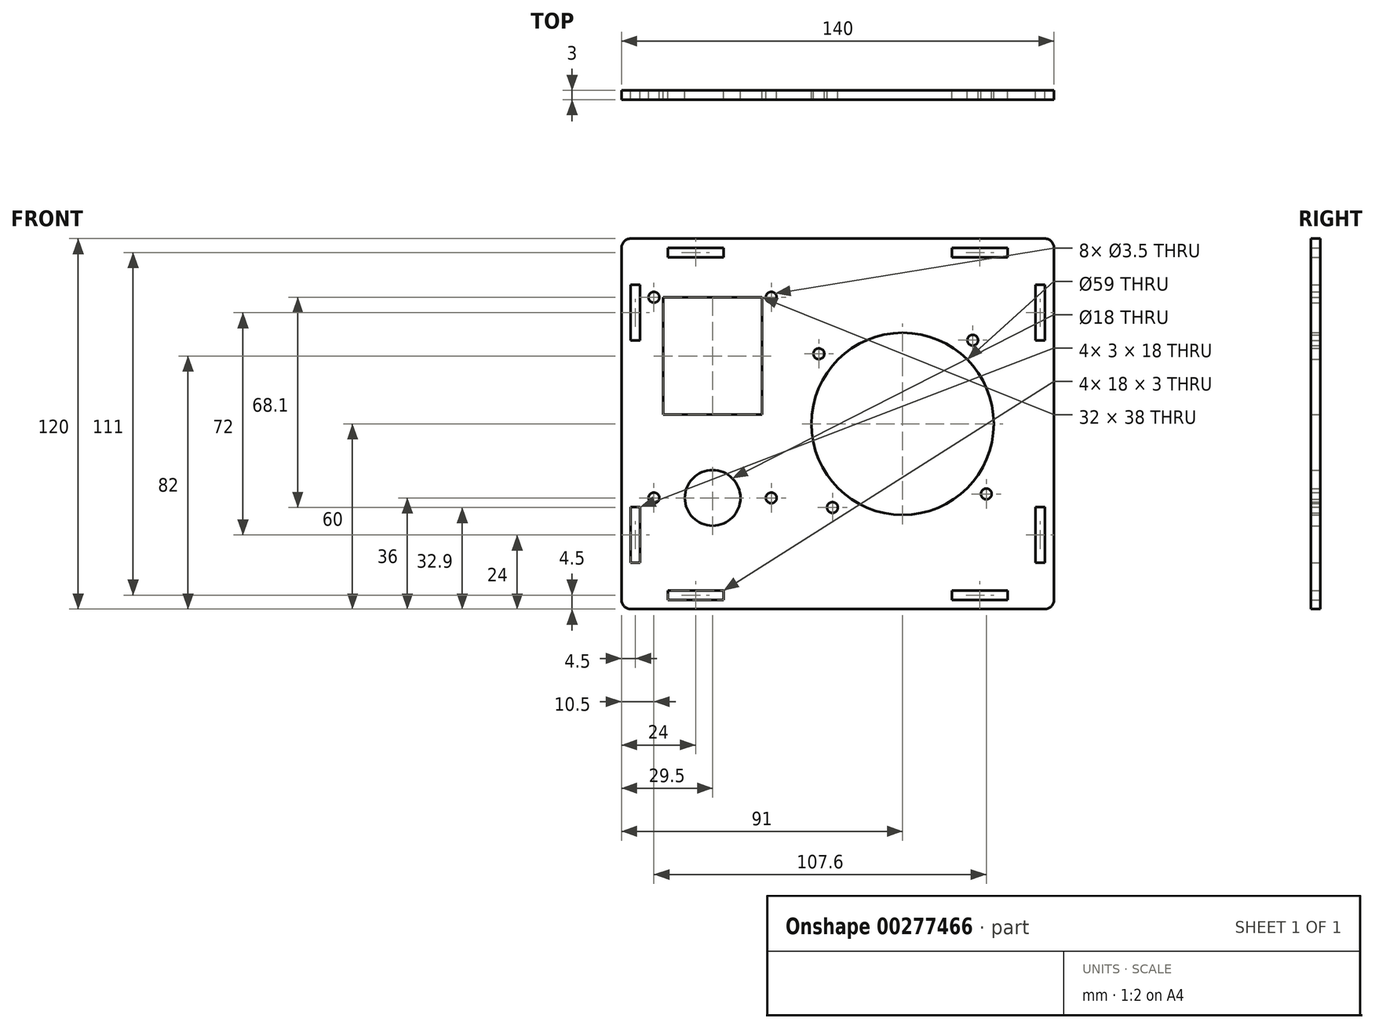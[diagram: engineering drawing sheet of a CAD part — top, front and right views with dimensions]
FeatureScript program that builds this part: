
annotation { "Feature Type Name" : "Feature", "Feature Type Description" : "" }
export const myFeature = defineFeature(function(context is Context, id is Id, definition is map)
    precondition{}
    {
        {
            var Q0;
            Q0=qCreatedBy(makeId("Front.planeOp"),FACE);
            var sketch = newSketch(context, id + "F0", { "sketchPlane" : qUnion([Q0])});
            skLineSegment(sketch, "E0.bottom", {"start": v(-67, 60) * mm, "end": v(67, 60) * mm});
            skLineSegment(sketch, "E0.top", {"start": v(-67, -60) * mm, "end": v(67, -60) * mm});
            skLineSegment(sketch, "E0.left", {"start": v(-70, 57) * mm, "end": v(-70, -57) * mm});
            skLineSegment(sketch, "E0.right", {"start": v(70, 57) * mm, "end": v(70, -57) * mm});
            skPoint(sketch, "E1.visualSharp", {"position": v(-70, 60) * mm});
            skArc(sketch, "E1.filletArc", {"start": v(-67, 60) * mm, "mid": v(-69.12, 59.12) * mm, "end": v(-70, 57) * mm});
            skPoint(sketch, "E2.visualSharp", {"position": v(70, 60) * mm});
            skArc(sketch, "E2.filletArc", {"start": v(70, 57) * mm, "mid": v(69.12, 59.12) * mm, "end": v(67, 60) * mm});
            skPoint(sketch, "E3.visualSharp", {"position": v(70, -60) * mm});
            skArc(sketch, "E3.filletArc", {"start": v(67, -60) * mm, "mid": v(69.12, -59.12) * mm, "end": v(70, -57) * mm});
            skPoint(sketch, "E4.visualSharp", {"position": v(-70, -60) * mm});
            skArc(sketch, "E4.filletArc", {"start": v(-70, -57) * mm, "mid": v(-69.12, -59.12) * mm, "end": v(-67, -60) * mm});
            skLineSegment(sketch, "E5.bottom", {"start": v(-55, 57) * mm, "end": v(-37, 57) * mm});
            skLineSegment(sketch, "E5.top", {"start": v(-55, 54) * mm, "end": v(-37, 54) * mm});
            skLineSegment(sketch, "E5.left", {"start": v(-55, 57) * mm, "end": v(-55, 54) * mm});
            skLineSegment(sketch, "E5.right", {"start": v(-37, 57) * mm, "end": v(-37, 54) * mm});
            skLineSegment(sketch, "E6.bottom", {"start": v(37, 57) * mm, "end": v(55, 57) * mm});
            skLineSegment(sketch, "E6.top", {"start": v(37, 54) * mm, "end": v(55, 54) * mm});
            skLineSegment(sketch, "E6.left", {"start": v(37, 57) * mm, "end": v(37, 54) * mm});
            skLineSegment(sketch, "E6.right", {"start": v(55, 57) * mm, "end": v(55, 54) * mm});
            skLineSegment(sketch, "E7.bottom", {"start": v(67, 45) * mm, "end": v(64, 45) * mm});
            skLineSegment(sketch, "E7.top", {"start": v(67, 27) * mm, "end": v(64, 27) * mm});
            skLineSegment(sketch, "E7.left", {"start": v(67, 45) * mm, "end": v(67, 27) * mm});
            skLineSegment(sketch, "E7.right", {"start": v(64, 45) * mm, "end": v(64, 27) * mm});
            skLineSegment(sketch, "E8.bottom", {"start": v(67, -27) * mm, "end": v(64, -27) * mm});
            skLineSegment(sketch, "E8.top", {"start": v(67, -45) * mm, "end": v(64, -45) * mm});
            skLineSegment(sketch, "E8.left", {"start": v(67, -27) * mm, "end": v(67, -45) * mm});
            skLineSegment(sketch, "E8.right", {"start": v(64, -27) * mm, "end": v(64, -45) * mm});
            skLineSegment(sketch, "E9.bottom", {"start": v(55, -57) * mm, "end": v(37, -57) * mm});
            skLineSegment(sketch, "E9.top", {"start": v(55, -54) * mm, "end": v(37, -54) * mm});
            skLineSegment(sketch, "E9.left", {"start": v(55, -57) * mm, "end": v(55, -54) * mm});
            skLineSegment(sketch, "E9.right", {"start": v(37, -57) * mm, "end": v(37, -54) * mm});
            skLineSegment(sketch, "E10.bottom", {"start": v(-37, -57) * mm, "end": v(-55, -57) * mm});
            skLineSegment(sketch, "E10.top", {"start": v(-37, -54) * mm, "end": v(-55, -54) * mm});
            skLineSegment(sketch, "E10.left", {"start": v(-37, -57) * mm, "end": v(-37, -54) * mm});
            skLineSegment(sketch, "E10.right", {"start": v(-55, -57) * mm, "end": v(-55, -54) * mm});
            skLineSegment(sketch, "E11.bottom", {"start": v(-64, -27) * mm, "end": v(-67, -27) * mm});
            skLineSegment(sketch, "E11.top", {"start": v(-64, -45) * mm, "end": v(-67, -45) * mm});
            skLineSegment(sketch, "E11.left", {"start": v(-64, -45) * mm, "end": v(-64, -27) * mm});
            skLineSegment(sketch, "E11.right", {"start": v(-67, -45) * mm, "end": v(-67, -27) * mm});
            skLineSegment(sketch, "E12.bottom", {"start": v(-64, 27) * mm, "end": v(-67, 27) * mm});
            skLineSegment(sketch, "E12.top", {"start": v(-64, 45) * mm, "end": v(-67, 45) * mm});
            skLineSegment(sketch, "E12.left", {"start": v(-64, 27) * mm, "end": v(-64, 45) * mm});
            skLineSegment(sketch, "E12.right", {"start": v(-67, 27) * mm, "end": v(-67, 45) * mm});
            skCircle(sketch, "E13", {"center": v(21, 0) * mm, "radius": 29.5 * mm});
            skCircle(sketch, "E14", {"center": v(43.7, 27.1) * mm, "radius": 1.75 * mm});
            skCircle(sketch, "E15", {"center": v(-6.1, 22.7) * mm, "radius": 1.75 * mm});
            skCircle(sketch, "E16", {"center": v(-1.7, -27.1) * mm, "radius": 1.75 * mm});
            skCircle(sketch, "E17", {"center": v(48.1, -22.7) * mm, "radius": 1.75 * mm});
            skLineSegment(sketch, "E18", {"start": v(-70, 0) * mm, "end": v(70, 0) * mm, "construction": true});
            skCircle(sketch, "E19", {"center": v(-40.5, -24) * mm, "radius": 9 * mm});
            skLineSegment(sketch, "E20", {"start": v(-17, -5.98) * mm, "end": v(-17, -18.14) * mm, "construction": true});
            skLineSegment(sketch, "E21.bottom", {"start": v(-56.5, 41) * mm, "end": v(-24.5, 41) * mm});
            skLineSegment(sketch, "E21.top", {"start": v(-56.5, 3) * mm, "end": v(-24.5, 3) * mm});
            skLineSegment(sketch, "E21.left", {"start": v(-56.5, 41) * mm, "end": v(-56.5, 3) * mm});
            skLineSegment(sketch, "E21.right", {"start": v(-24.5, 41) * mm, "end": v(-24.5, 3) * mm});
            skLineSegment(sketch, "E22", {"start": v(-40.5, -24) * mm, "end": v(-40.5, -20.92) * mm, "construction": true});
            skCircle(sketch, "E23", {"center": v(-59.5, 41) * mm, "radius": 1.75 * mm});
            skCircle(sketch, "E24", {"center": v(-21.5, 41) * mm, "radius": 1.75 * mm});
            skCircle(sketch, "E25", {"center": v(-59.5, -24) * mm, "radius": 1.75 * mm});
            skCircle(sketch, "E26", {"center": v(-21.5, -24) * mm, "radius": 1.75 * mm});
            skSolve(sketch);
        }
        {
            var Q0;
            Q0=makeQuery(id+"F0.imprint","IMPRINT",FACE,{"disambiguationData":[TD([[makeQuery(id+"F0.imprint","IMPRINT",EDGE,{"derivedFrom":sQuery(id+"F0.wireOp",EDGE,"E0.bottom")}),-1.0]])]});
            extrude(context, id + "F1", {"entities" : qUnion([Q0]), "depth" : 3 * mm});
        }
    });
